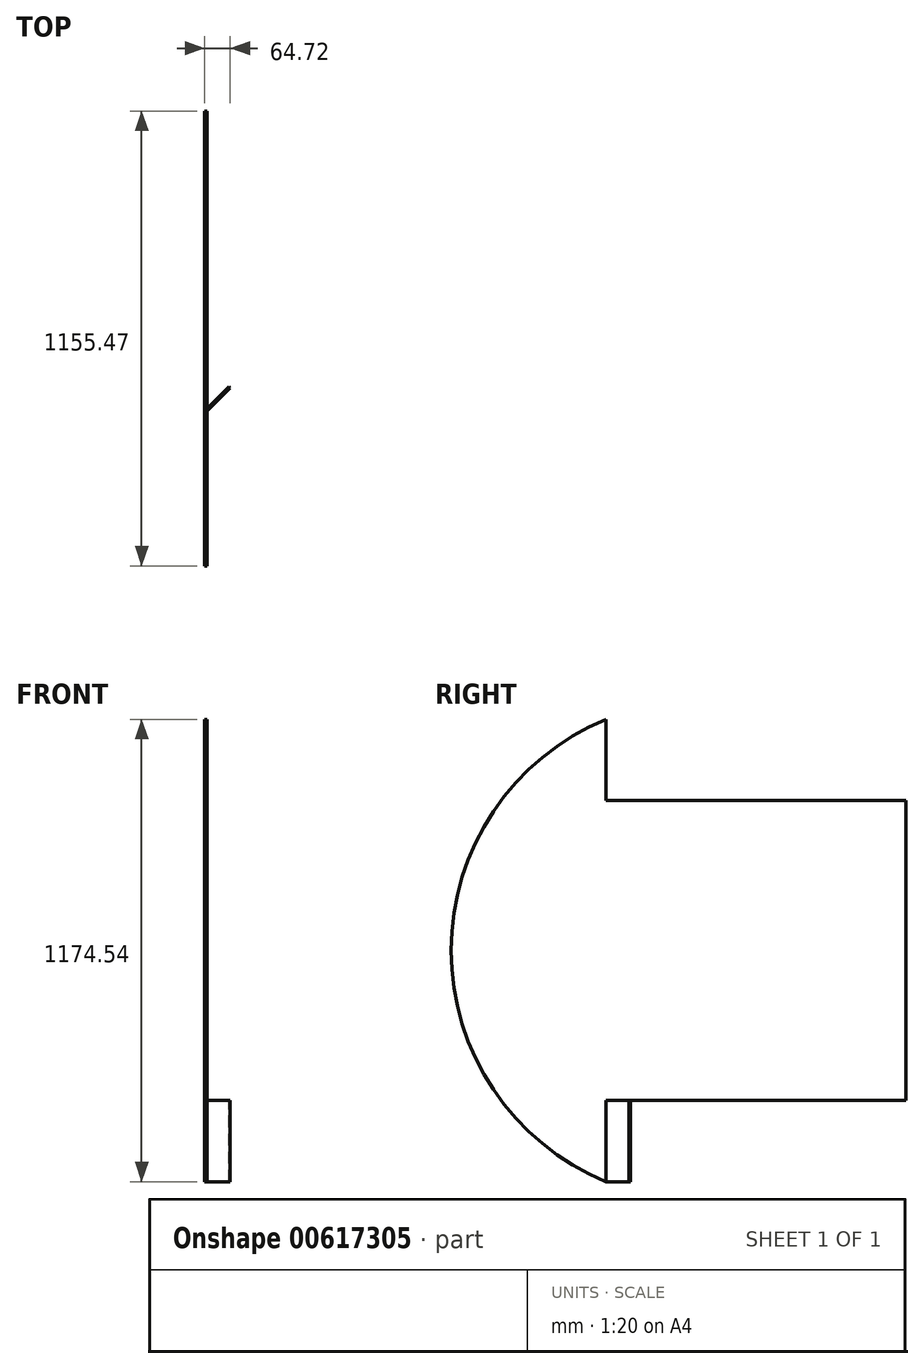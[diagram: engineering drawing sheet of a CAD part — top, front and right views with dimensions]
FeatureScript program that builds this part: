
annotation { "Feature Type Name" : "Feature", "Feature Type Description" : "" }
export const myFeature = defineFeature(function(context is Context, id is Id, definition is map)
    precondition{}
    {
        {
            var Q0;
            Q0=qCreatedBy(makeId("Right.planeOp"),FACE);
            var sketch = newSketch(context, id + "F0", { "sketchPlane" : qUnion([Q0])});
            skLineSegment(sketch, "E0.bottom", {"start": v(0, 0) * mm, "end": v(762, 0) * mm});
            skLineSegment(sketch, "E0.top", {"start": v(0, 762) * mm, "end": v(762, 762) * mm});
            skLineSegment(sketch, "E0.right", {"start": v(762, 0) * mm, "end": v(762, 762) * mm});
            skLineSegment(sketch, "E1.left", {"start": v(0, 968.27) * mm, "end": v(0, 762) * mm, "construction": true});
            skPoint(sketch, "E1.middle", {"position": v(-155.36, 381) * mm});
            skArc(sketch, "E2", {"start": v(0, 968.27) * mm, "mid": v(-393.47, 381) * mm, "end": v(0, -206.27) * mm});
            skLineSegment(sketch, "E3", {"start": v(0, 968.27) * mm, "end": v(0, 762) * mm});
            skPoint(sketch, "E4.orphan", {"position": v(-310.73, 968.27) * mm});
            skPoint(sketch, "E1.top.end.orphan", {"position": v(-310.73, -206.27) * mm});
            skLineSegment(sketch, "E5.trimOffspring", {"start": v(0, 0) * mm, "end": v(0, -206.27) * mm, "construction": true});
            skLineSegment(sketch, "E6.trimOffspring", {"start": v(0, 0) * mm, "end": v(0, -206.27) * mm});
            skPoint(sketch, "E7.orphan", {"position": v(0, 381) * mm});
            skPoint(sketch, "E8.end.orphan", {"position": v(-393.47, 381) * mm});
            skPoint(sketch, "E9.start.orphan", {"position": v(762, 381) * mm});
            skSolve(sketch);
        }
        {
            var Q0;
            Q0=makeQuery(id+"F0.imprint","IMPRINT",FACE,{"disambiguationData":[TD([[makeQuery(id+"F0.imprint","IMPRINT",EDGE,{"derivedFrom":sQuery(id+"F0.wireOp",EDGE,"E0.bottom")}),1.0]])]});
            extrude(context, id + "F1", {"entities" : qUnion([Q0]), "depth" : 6.35 * mm, "offsetDistance" : 25.4 * mm});
        }
        {
            var Q0;
            Q0=makeQuery(id+"F1.opExtrude","SWEPT_FACE",FACE,{"disambiguationData":[OSD([sQuery(id+"F0.wireOp",EDGE,"E0.bottom")])]});
            var sketch = newSketch(context, id + "F2", { "sketchPlane" : qUnion([Q0])});
            skLineSegment(sketch, "E10", {"start": v(6.35, 0) * mm, "end": v(64.72, -58.37) * mm});
            skLineSegment(sketch, "E11", {"start": v(64.72, -58.37) * mm, "end": v(61.5, -61.6) * mm});
            skLineSegment(sketch, "E12", {"start": v(61.5, -61.6) * mm, "end": v(6.35, -6.44) * mm});
            skLineSegment(sketch, "E13", {"start": v(6.35, -6.44) * mm, "end": v(0, 0) * mm});
            skLineSegment(sketch, "E14", {"start": v(0, 0) * mm, "end": v(6.35, 0) * mm});
            skSolve(sketch);
        }
        {
            var Q0;
            Q0 = qSketchRegion(id + "F2", true);
            var Q1;
            Q1=sQuery(id+"F0.wireOp",VERTEX,"E2.end");
            extrude(context, id + "F3", {"entities" : qUnion([Q0]), "endBound" : BoundingType.UP_TO_VERTEX, "depth" : 208.28 * mm, "endBoundEntityVertex" : qUnion([Q1]), "offsetDistance" : 25.4 * mm});
        }
    });
